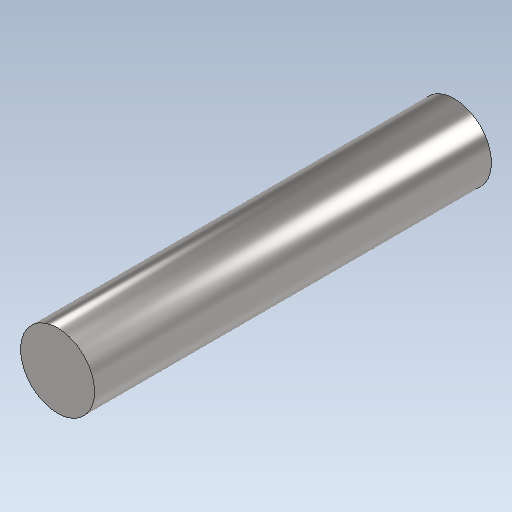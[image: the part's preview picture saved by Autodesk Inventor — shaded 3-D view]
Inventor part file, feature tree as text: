
AUTODESK INVENTOR PART (.ipt)
format: ipt  version: 2023 (Build 270158000, 158)  size: 116,736 bytes
history: native  units: in
note: dims shown in document units (in); Inventor stores cm internally (conversion verified against a paired STEP export)
features: other x3, sketch x1
ambient origin geometry x8: Origin, YZ Plane, XZ Plane, XY Plane, X Axis, Y Axis, Z Axis, Center Point
bodies: Solid1 (feature_tree)
feature tree (4):
  other  "CH-1-01-0.25x1.875SmoothShaft.ipt"
  other  "Solid1::CH-1-01-0.25x1.875SmoothShaft.ipt"
  other  "TaggingFeature1"
  sketch  "Sketch1"  dims[d0=0.3937in]
